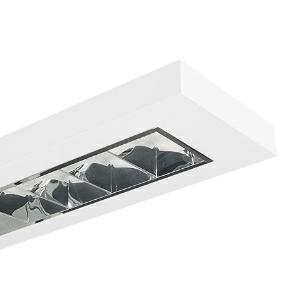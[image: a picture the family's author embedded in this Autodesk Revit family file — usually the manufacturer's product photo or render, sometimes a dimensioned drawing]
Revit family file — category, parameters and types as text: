
# Revit family: 3f_filippi_-_3f_travetta_di_2mg_3f_filippi_-_11504_-_3f_travetta_led_di_2x22w_dali_2mg_l1590
name_source: partatom
category: Lighting Fixtures
units: mm (PartAtom-declared; Revit-internal decimal feet)

## family parameters
Cut with Voids When Loaded = No
Host = Face
Light Source = No
Part Type = Normal
Room Calculation Point = No
Round Connector Dimension = Use Diameter
Shared = No

## types (1)
- 3F Filippi - 3F Travetta DI 2MG (1 x LED, 5865 lm, 49 W, 4000 K)
    Apparent Load = 49 VA
    Approval mark = ENEC
    CIE Flux Codes = 61 98 100 85 100
    Color Rendering = 80
    Color Temperature = 4000 K
    Control Gear = Electronic transformer
    Default Elevation = 1800 mm
    Description = ILLUMINOTECHNICAL
Luminous efficiency 100% (DLOR 85%, ULOR 15%).
Initial luminous flux of the luminaire 5865 lm.
Symmetric direct-indirect distribution.
Installation Interdistance Transv.D = 2.02 x hu - Long.D = 1.27 x hu.
Average luminance <1000 cd/m² for radial angles >65°.
Tabular UGR (CIE 117 - 4H-8H; S=0.25H; 70/50/20): RUG 18.4 - 17.8.
Beam angle: 99° - 72°.
Luminous efficacy 120 lm/W.
Lifetime (L93/B10): 30000 h. (tq+25°C)
Lifetime (L90/B10): 50000 h. (tq+25°C)
Lifetime (L85/B10): 80000 h. (tq+25°C)
Lifetime (L80/B10): 100000 h. (tq+25°C)
Sudden decreased luminous flux after 50000 hours: 0% (C0).
Photobiological safety in compliance with IEC/TR 62778: RG0 risk exempt, (IEC 62471).
In compliance with IEC/EN 62722-2-1 - IEC/EN 62717 standards.

SOURCE
2 linear LED modules 22W/840.
Energy efficiency class (UE 2019/2020 - UE 2019/2015): D.
CIE 13.3 Colour rendering index: CRI >80 (R9 <50%).
IES TM-30 Fidelity Index: Rf = 84 Rg = 95.
CCT nominal colour temperature 4000 K.
Colour initial tolerance (MacAdam): SDCM 2.

MECHANICAL
Housing with squared shape in white painted galvannealed steel, with nonreflecting surface.
2MG parabolic louvre, high efficiency, in specular aluminium with superficial titanium-magnesium treatment, non-iridescent, with transverse blades closed at the top.
Prismatic flat diffuser in transparent methacrylate (PMMA), multilenticular, anti-glare, prismatic exterior, placed above louvre blades.
Film protective against dust and finger marks, adhesive, attached to louvre.
Upper holes closing film made of opal polycarbonate.
Luminaire with limited surface temperature. - D - (EN 60598-2-24)
Dimensions: 1590x190 mm, height 60 mm (edge 40 mm). Weight 5.015 kg.
IP20 protection degree.
Mechanical strength to impacts IK02 (0.2 joule).
Glow-wire test resistance 650°C.

ELECTRICAL
Halogen Free DALI-2 DATI (Parts 251, 252, 253), PUSH-DIM, electronic wiring 230V-50/60Hz, power factor 0.95 at full load, THD <25%, constant output current, SELV, class I, 1 driver, 1 DALI addresse.
Power of the luminaire 49 W.
CE - IEC 60598-1 - EN 60598-1.
SAFE FLICKER: PstLM=<1 and SVM=<0.4 (IEC TR 61547-1 and IEC TR 63158), to ensure a more comfortable and safe light.
Luminaire compliant with EN 60598-2-22 for power supply from a centralised emergency system CPSS (Central Power Supply System), not incorporated in the luminaire - high risk areas excluded. The default power and flux are 100% in AC and 15% in DC.
Ambient temperature from 0°C to +25°C.
Temperature class T6 max 85°C.
Relative humidity UR: <85%.

INSTALLATION
Suspended.
All accessories dedicated to this product are available on the Catalog and on our website www.3F-Filippi.com.

APPLICATIONS
In environments, even with reduced height, requiring a comfortable light.
In environments with VDTs, managerial offices and staterooms, public offices and schools.

LIGHT MANAGEMENT
Recommended minimum setting: 10%.
The luminaire, equipped with (DALI-2 DATI) driver, can be controlled manually with 3F Easy Dim technology or automatically/manually with wired or wireless DALI/D2D control systems.
The D2D driver guarantees interoperability with other devices with the same certification by making the following information available:
Device Data (Part 251), Energy Report (Part 252), Diagnosis & Maintenance (Part 253).
In electrical systems without a regulation system (manual or automatic) and DALI bus, a suitable jumper must be made on the DA-DA terminals of the appliance.

WARNING
Luminaire designed for disposal/recycling at end-of-life.
Replaceable (LED only) light source by a professional. Replaceable control gear by a professional.
    Height = 60 mm  [stored 0.19685 ft]
    Lamp = 1 x LED
    Lamp Light Flux = 5865 lm
    Lamp Power = 49 W
    Lamp count = 1
    Length = 1590 mm
    Lifetime = 50000 h
    Luminous efficacy = 120 lm/W
    Manufacturer = 3F Filippi
    ModVariant = No
    Model = 3F Filippi - 11504 - 3F Travetta LED DI 2x22W DALI 2MG L1590
    Mounting Place = Ceiling
    Mounting Type = Pendant
    Number of Poles = 1
    OnlyDefault = Yes
    Power Factor = 1
    Product Name = 3F Filippi - 3F Travetta DI 2MG
    Product group = pendant luminaire
    ProductGroupID = 9
    Protection Class = Protection class I
    Protection Degree = IP 20
    RLX_Detail_Level = 1
    RLX_Emergency_Light_Flux = 0 lm
    RLX_Emergency_Type = 0
    RLX_Emergency_Type_DB = No
    RlxData = <blob elided: 53677 chars, md5=f0474942>
    Socket = socket
    Standby Power = 0 W
    System Light Flux = 5865 lm
    System Power = 49 W
    Type Comments = Product without accessories
    Type Image = 3ffilippi_3f_travetta_led_2mg.jpg
    URL = http://relux.com
    VarID = ---
    Voltage = 0 V
    Weight = 0.00 kg
    Width = 190 mm  [stored 0.62336 ft]

note: [stored X ft] marks values corroborated as IEEE doubles in the binary element streams (Revit-internal decimal feet)

## geometry (parser evidence)
native form markers: Blend x4, Sweep x11
no freeform markers — native parametric forms only
